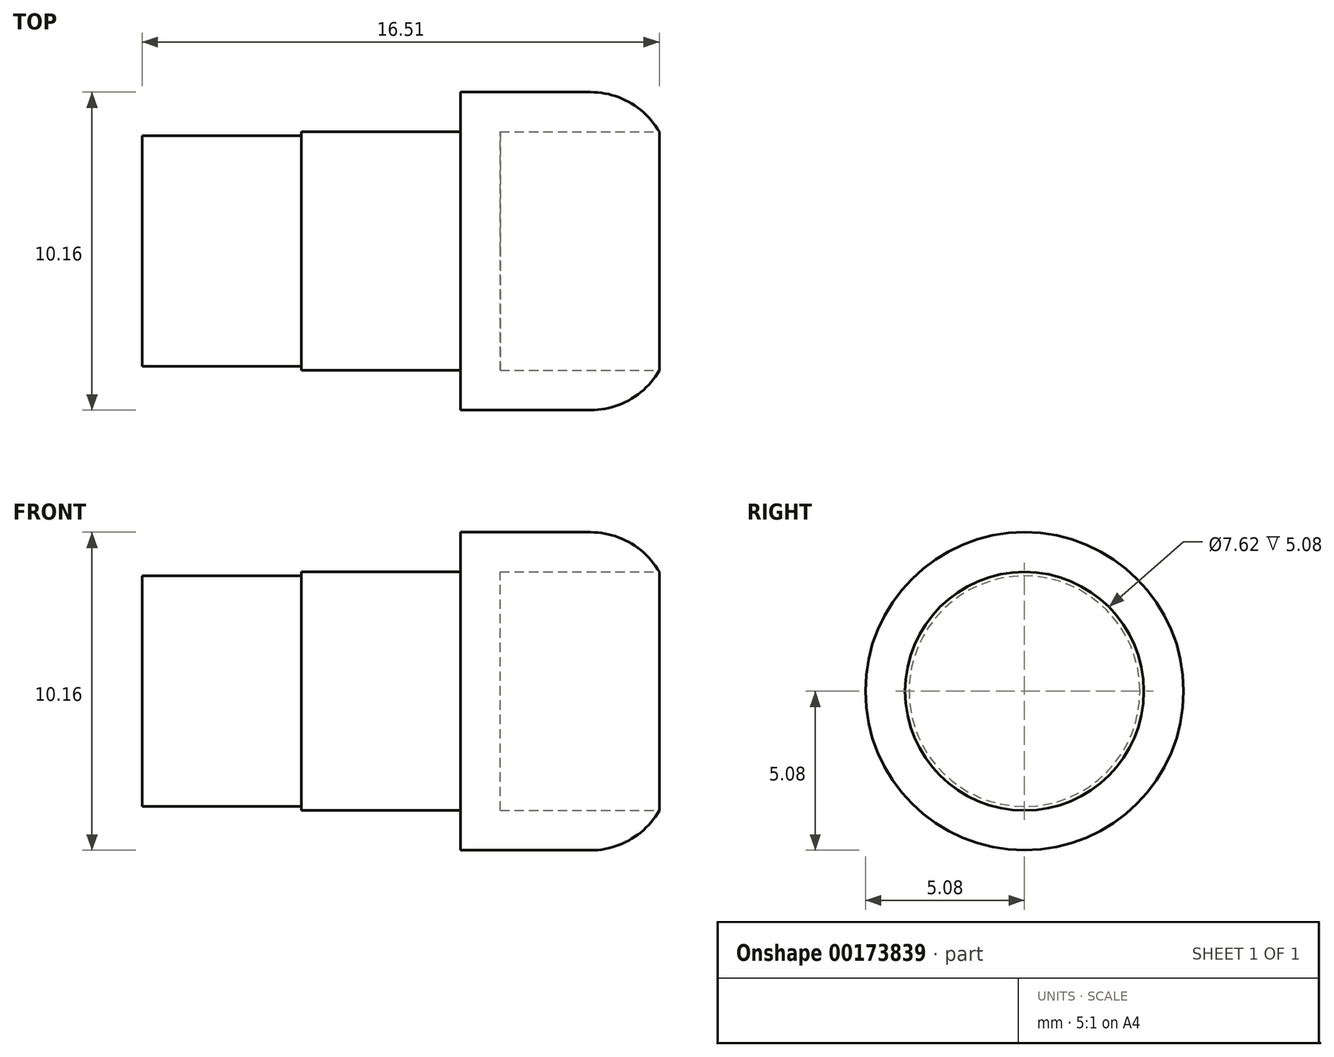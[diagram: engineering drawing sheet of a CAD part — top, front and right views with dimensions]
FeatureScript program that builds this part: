
annotation { "Feature Type Name" : "Feature", "Feature Type Description" : "" }
export const myFeature = defineFeature(function(context is Context, id is Id, definition is map)
    precondition{}
    {
        {
            var Q0;
            Q0=qCreatedBy(makeId("Right.planeOp"),FACE);
            var sketch = newSketch(context, id + "F0", { "sketchPlane" : qUnion([Q0])});
            skCircle(sketch, "E0", {"center": v(0, 0) * mm, "radius": 5.08 * mm});
            skSolve(sketch);
        }
        {
            var Q0;
            Q0 = qSketchRegion(id + "F0", true);
            extrude(context, id + "F1", {"entities" : qUnion([Q0]), "depth" : 17.78 * mm});
        }
        {
            var Q0;
            Q0=makeQuery(id+"F1.opExtrude","CAP_FACE",FACE,{"disambiguationData":[OSD([sQuery(id+"F0.wireOp",EDGE,"E0")])],"isStart":true});
            var sketch = newSketch(context, id + "F2", { "sketchPlane" : qUnion([Q0])});
            skCircle(sketch, "E1", {"center": v(0, 0) * mm, "radius": 3.68 * mm});
            skSolve(sketch);
        }
        {
            var Q0;
            Q0=makeQuery(id+"F2.imprint","IMPRINT",FACE,{"disambiguationData":[TD([[makeQuery(id+"F2.imprint","IMPRINT",EDGE,{"derivedFrom":sQuery(id+"F2.wireOp",EDGE,"E1")}),-1.0]])]});
            extrude(context, id + "F3", {"entities" : qUnion([Q0]), "operationType" : NewBodyOperationType.REMOVE, "oppositeDirection" : true, "depth" : 6.35 * mm});
        }
        {
            var Q0;
            Q0=makeQuery(id+"F3.boolean.opBoolean","COPY",FACE,{"derivedFrom":makeQuery(id+"F3.opExtrude","CAP_FACE",FACE,{"disambiguationData":[OSD([sQuery(id+"F0.wireOp",EDGE,"E0"),sQuery(id+"F2.wireOp",EDGE,"E1")])],"isStart":false})});
            var sketch = newSketch(context, id + "F4", { "sketchPlane" : qUnion([Q0])});
            skCircle(sketch, "E2", {"center": v(0, 0) * mm, "radius": 3.81 * mm});
            skCircle(sketch, "E3", {"center": v(0, 0) * mm, "radius": 5.08 * mm});
            skSolve(sketch);
        }
        {
            var Q0;
            Q0=makeQuery(id+"F4.imprint","IMPRINT",FACE,{"disambiguationData":[TD([[makeQuery(id+"F4.imprint","IMPRINT",EDGE,{"derivedFrom":sQuery(id+"F4.wireOp",EDGE,"E2")}),-1.0]])]});
            extrude(context, id + "F5", {"entities" : qUnion([Q0]), "operationType" : NewBodyOperationType.REMOVE, "oppositeDirection" : true, "depth" : 5.08 * mm});
        }
        {
            var Q0;
            Q0=makeQuery(id+"F1.opExtrude","CAP_FACE",FACE,{"disambiguationData":[OSD([sQuery(id+"F0.wireOp",EDGE,"E0")])],"isStart":false});
            var sketch = newSketch(context, id + "F6", { "sketchPlane" : qUnion([Q0])});
            skCircle(sketch, "E4", {"center": v(0, 0) * mm, "radius": 3.8 * mm});
            skSolve(sketch);
        }
        {
            var Q0;
            Q0 = qSketchRegion(id + "F6", true);
            extrude(context, id + "F7", {"entities" : qUnion([Q0]), "operationType" : NewBodyOperationType.REMOVE, "oppositeDirection" : true, "depth" : 5.08 * mm});
        }
        {
            var Q0;
            Q0=makeQuery(id+"F1.opExtrude","CAP_FACE",FACE,{"disambiguationData":[OSD([sQuery(id+"F0.wireOp",EDGE,"E0")])],"isStart":true});
            var sketch = newSketch(context, id + "F8", { "sketchPlane" : qUnion([Q0])});
            skCircle(sketch, "E5", {"center": v(0, 0) * mm, "radius": 3.68 * mm});
            skSolve(sketch);
        }
        {
            var Q0;
            Q0 = qSketchRegion(id + "F8", true);
            extrude(context, id + "F9", {"entities" : qUnion([Q0]), "operationType" : NewBodyOperationType.REMOVE, "oppositeDirection" : true, "depth" : 1.27 * mm});
        }
        {
            var Q0;
            Q0=makeQuery(id+"F1.opExtrude","CAP_EDGE",EDGE,{"disambiguationData":[OSD([sQuery(id+"F0.wireOp",EDGE,"E0")])],"isStart":false});
            fillet(context, id + "F10", {"entities" : qUnion([Q0]), "radius" : 2.54 * mm, "tangentPropagation" : true, "allowEdgeOverflow" : false});
        }
    });
